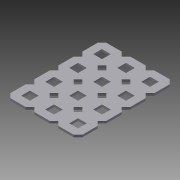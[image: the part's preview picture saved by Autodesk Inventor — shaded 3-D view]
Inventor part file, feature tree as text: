
AUTODESK INVENTOR PART (.ipt)
format: ipt  version: 2012 (Build 160160000, 160)  size: 1,056,256 bytes
history: native  units: in
note: dims shown in document units (in); Inventor stores cm internally (conversion verified against a paired STEP export)
features: sketch x2, other x1, imported_body x1, extrude x1, plane x1, split x1
ambient origin geometry x8: Origin, YZ Plane, XZ Plane, XY Plane, X Axis, Y Axis, Z Axis, Center Point
feature tree (7):
  parser-record x1  (decoder bookkeeping rows leaked as tree rows — omitted from the tree; the rows remain in map.json)
  imported_body  "Base1"
  sketch  "Sketch1"  dims[d0=3.937in d2=0.5in d3=1.9685in d5=0.5in d10=1.0in d11=0.0in]
  extrude  "Extrusion1"  Depth=1.0in TaperAngle=0.0deg
  plane  "Work Plane1"
  split  "Split1"
  sketch  "Sketch3"  dims[d12=-1.0in]
